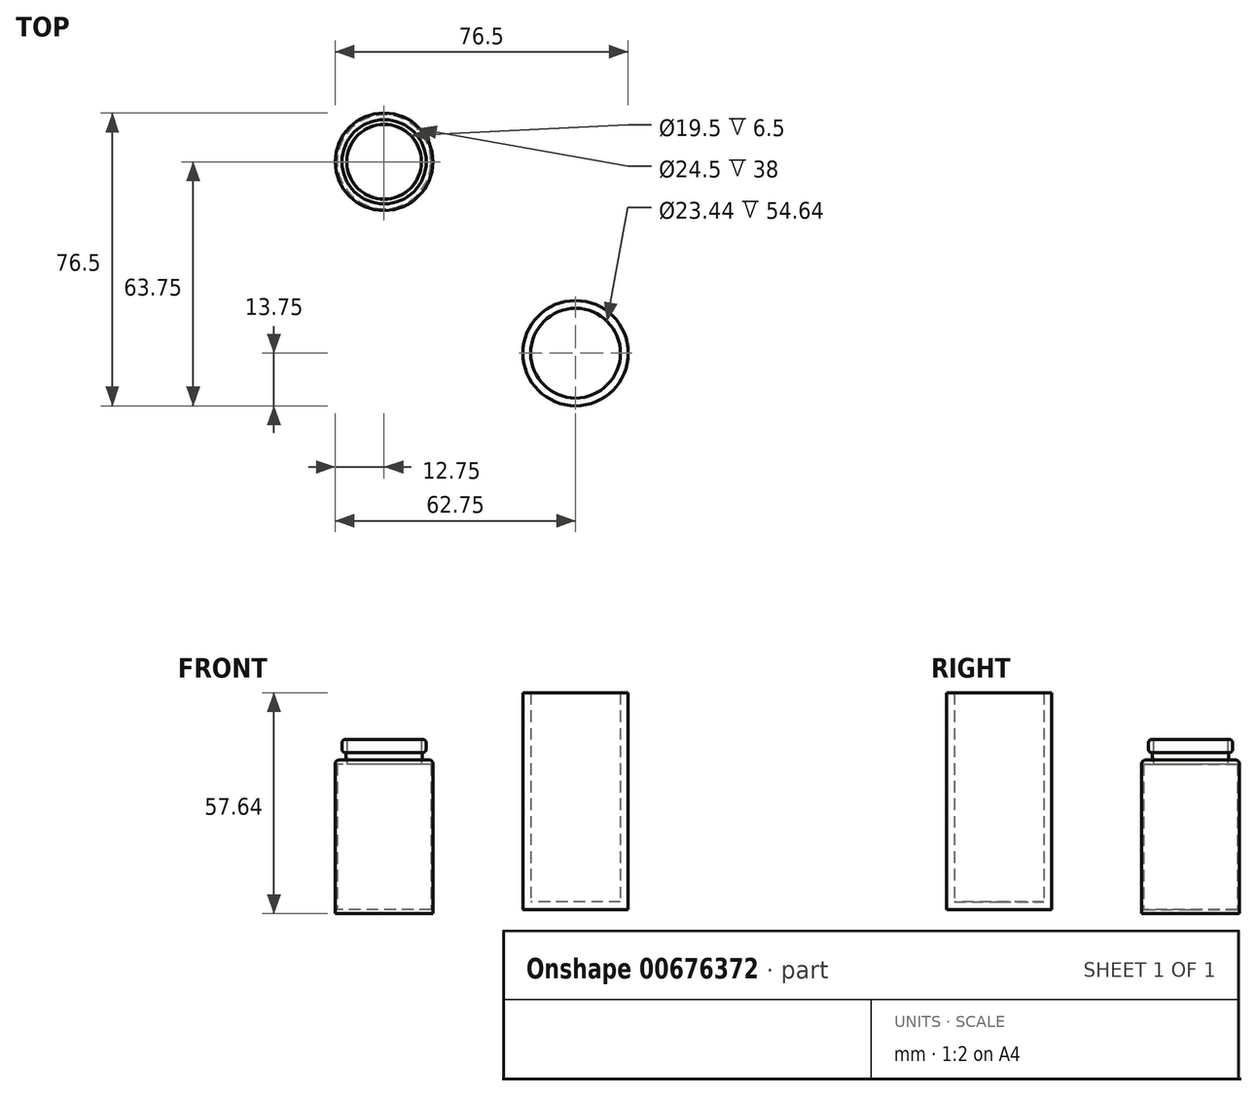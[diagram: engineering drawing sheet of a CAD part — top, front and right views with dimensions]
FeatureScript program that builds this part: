
annotation { "Feature Type Name" : "Feature", "Feature Type Description" : "" }
export const myFeature = defineFeature(function(context is Context, id is Id, definition is map)
    precondition{}
    {
        {
            var Q0;
            Q0=qCreatedBy(makeId("Top.planeOp"),FACE);
            var sketch = newSketch(context, id + "F0", { "sketchPlane" : qUnion([Q0])});
            skCircle(sketch, "E0", {"center": v(0, 0) * mm, "radius": 13.75 * mm});
            skCircle(sketch, "E1", {"center": v(0, 0) * mm, "radius": 11.72 * mm});
            skSolve(sketch);
        }
        {
            var Q0;
            Q0=makeQuery(id+"F0.imprint","IMPRINT",FACE,{"disambiguationData":[TD([[makeQuery(id+"F0.imprint","IMPRINT",EDGE,{"derivedFrom":sQuery(id+"F0.wireOp",EDGE,"E0")}),1.0]])]});
            var Q1;
            Q1=makeQuery(id+"F0.imprint","IMPRINT",FACE,{"disambiguationData":[TD([[makeQuery(id+"F0.imprint","IMPRINT",EDGE,{"derivedFrom":sQuery(id+"F0.wireOp",EDGE,"E1")}),1.0]])]});
            extrude(context, id + "F1", {"entities" : qUnion([Q0, Q1]), "depth" : 2 * mm, "offsetDistance" : 25 * mm});
        }
        {
            var Q0;
            Q0=makeQuery(id+"F0.imprint","IMPRINT",FACE,{"disambiguationData":[TD([[makeQuery(id+"F0.imprint","IMPRINT",EDGE,{"derivedFrom":sQuery(id+"F0.wireOp",EDGE,"E0")}),1.0]])]});
            extrude(context, id + "F2", {"entities" : qUnion([Q0]), "operationType" : NewBodyOperationType.ADD, "depth" : 56.64 * mm, "offsetDistance" : 25 * mm});
        }
        {
            var Q0;
            Q0=qCreatedBy(makeId("Top.planeOp"),FACE);
            var sketch = newSketch(context, id + "F3", { "sketchPlane" : qUnion([Q0])});
            skLineSegment(sketch, "E2", {"start": v(-127.25, 50) * mm, "end": v(94.88, 50) * mm, "construction": true});
            skLineSegment(sketch, "E3", {"start": v(-50, 62.51) * mm, "end": v(-50, -43.4) * mm, "construction": true});
            skCircle(sketch, "E4", {"center": v(-50, 50) * mm, "radius": 12.75 * mm});
            skCircle(sketch, "E5", {"center": v(-50, 50) * mm, "radius": 12.25 * mm});
            skSolve(sketch);
        }
        {
            var Q0;
            Q0=makeQuery(id+"F3.imprint","IMPRINT",FACE,{"disambiguationData":[TD([[makeQuery(id+"F3.imprint","IMPRINT",EDGE,{"derivedFrom":sQuery(id+"F3.wireOp",EDGE,"E4")}),1.0]])]});
            extrude(context, id + "F4", {"entities" : qUnion([Q0]), "depth" : 38 * mm, "offsetDistance" : 25 * mm, "hasSecondDirection" : true, "secondDirectionOppositeDirection" : true, "secondDirectionDepth" : 1 * mm});
        }
        {
            var Q0;
            Q0=makeQuery(id+"F3.imprint","IMPRINT",FACE,{"disambiguationData":[TD([[makeQuery(id+"F3.imprint","IMPRINT",EDGE,{"derivedFrom":sQuery(id+"F3.wireOp",EDGE,"E5")}),1.0]])]});
            extrude(context, id + "F5", {"entities" : qUnion([Q0]), "operationType" : NewBodyOperationType.ADD, "oppositeDirection" : true, "depth" : 1 * mm, "offsetDistance" : 25 * mm});
        }
        {
            var Q0;
            Q0=makeQuery(id+"F4.opExtrude","CAP_FACE",FACE,{"disambiguationData":[OSD([sQuery(id+"F3.wireOp",EDGE,"E4"),sQuery(id+"F3.wireOp",EDGE,"E5")])],"isStart":false});
            var sketch = newSketch(context, id + "F6", { "sketchPlane" : qUnion([Q0])});
            skCircle(sketch, "E6", {"center": v(-50, 50) * mm, "radius": 10 * mm});
            skCircle(sketch, "E7", {"center": v(-50, 50) * mm, "radius": 12.75 * mm});
            skCircle(sketch, "E8", {"center": v(-50, 50) * mm, "radius": 9.75 * mm});
            skSolve(sketch);
        }
        {
            var Q0;
            Q0=qSketchRegion(id+"F6",true);
            var Q1;
            Q1=makeQuery(id+"F6.imprint","IMPRINT",FACE,{"disambiguationData":[TD([[makeQuery(id+"F6.imprint","IMPRINT",EDGE,{"derivedFrom":sQuery(id+"F6.wireOp",EDGE,"E6")}),1.0]])]});
            extrude(context, id + "F7", {"entities" : qUnion([Q0, Q1]), "operationType" : NewBodyOperationType.ADD, "depth" : 1.1 * mm, "offsetDistance" : 25 * mm});
        }
        {
            var Q0;
            Q0=makeQuery(id+"F6.imprint","IMPRINT",FACE,{"disambiguationData":[TD([[makeQuery(id+"F6.imprint","IMPRINT",EDGE,{"derivedFrom":sQuery(id+"F6.wireOp",EDGE,"E6")}),1.0]])]});
            extrude(context, id + "F8", {"entities" : qUnion([Q0]), "operationType" : NewBodyOperationType.ADD, "depth" : 3 * mm, "offsetDistance" : 25 * mm});
        }
        {
            var Q0;
            Q0=makeQuery(id+"F8.opExtrude","CAP_FACE",FACE,{"disambiguationData":[OSD([sQuery(id+"F6.wireOp",EDGE,"E6"),sQuery(id+"F6.wireOp",EDGE,"E8")])],"isStart":false});
            var sketch = newSketch(context, id + "F9", { "sketchPlane" : qUnion([Q0])});
            skCircle(sketch, "E9", {"center": v(-50, 50) * mm, "radius": 11 * mm});
            skCircle(sketch, "E10", {"center": v(-50, 50) * mm, "radius": 10 * mm});
            skCircle(sketch, "E11", {"center": v(-50, 50) * mm, "radius": 9.75 * mm});
            skSolve(sketch);
        }
        {
            var Q0;
            Q0=qSketchRegion(id+"F9",true);
            var Q1;
            Q1=makeQuery(id+"F9.imprint","IMPRINT",FACE,{"disambiguationData":[TD([[makeQuery(id+"F9.imprint","IMPRINT",EDGE,{"derivedFrom":sQuery(id+"F9.wireOp",EDGE,"E10")}),1.0]])]});
            extrude(context, id + "F10", {"entities" : qUnion([Q0, Q1]), "operationType" : NewBodyOperationType.ADD, "depth" : 3.5 * mm, "offsetDistance" : 25 * mm});
        }
        {
            var Q0;
            Q0=makeQuery(id+"F7.opExtrude","CAP_EDGE",EDGE,{"disambiguationData":[OSD([sQuery(id+"F6.wireOp",EDGE,"E7")])],"isStart":false});
            fillet(context, id + "F11", {"entities" : qUnion([Q0]), "radius" : 1 * mm, "tangentPropagation" : true, "allowEdgeOverflow" : false});
        }
        {
            var Q0;
            Q0=makeQuery(id+"F10.opExtrude","CAP_EDGE",EDGE,{"disambiguationData":[OSD([sQuery(id+"F9.wireOp",EDGE,"E9")])],"isStart":true});
            var Q1;
            Q1=makeQuery(id+"F10.opExtrude","CAP_EDGE",EDGE,{"disambiguationData":[OSD([sQuery(id+"F9.wireOp",EDGE,"E9")])],"isStart":false});
            fillet(context, id + "F12", {"entities" : qUnion([Q0, Q1]), "radius" : 1 * mm, "tangentPropagation" : true, "allowEdgeOverflow" : false});
        }
    });
